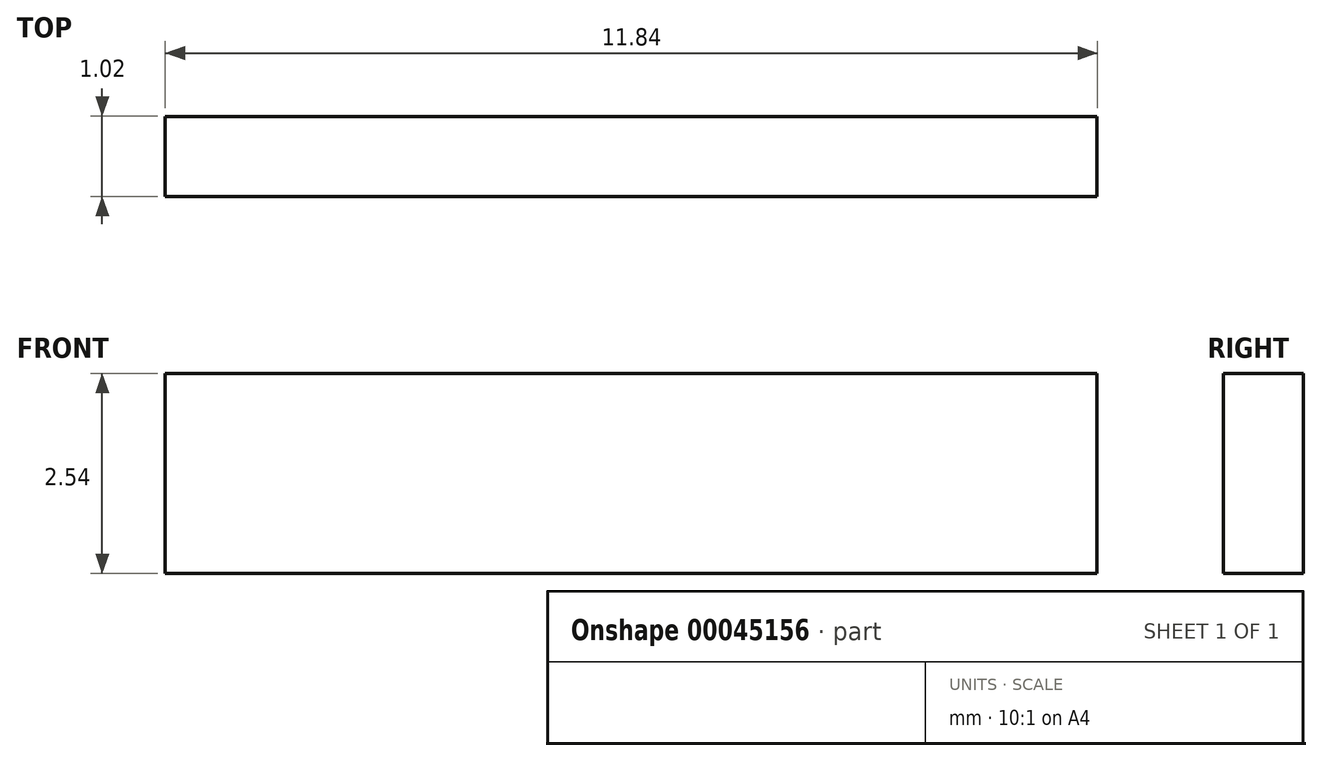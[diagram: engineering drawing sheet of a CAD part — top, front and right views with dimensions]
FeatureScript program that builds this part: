
annotation { "Feature Type Name" : "Feature", "Feature Type Description" : "" }
export const myFeature = defineFeature(function(context is Context, id is Id, definition is map)
    precondition{}
    {
        {
            var Q0;
            Q0=qCreatedBy(makeId("Top.planeOp"),FACE);
            var sketch = newSketch(context, id + "F0", { "sketchPlane" : qUnion([Q0])});
            skLineSegment(sketch, "E0", {"start": v(0, 0) * mm, "end": v(11.84, 0) * mm});
            skLineSegment(sketch, "E1", {"start": v(11.84, 0) * mm, "end": v(11.84, 1.02) * mm});
            skLineSegment(sketch, "E2", {"start": v(11.84, 1.02) * mm, "end": v(0, 1.02) * mm});
            skLineSegment(sketch, "E3", {"start": v(0, 1.02) * mm, "end": v(0, 0) * mm});
            skSolve(sketch);
        }
        {
            var Q0;
            Q0 = qSketchRegion(id + "F0", true);
            extrude(context, id + "F1", {"entities" : qUnion([Q0]), "depth" : 2.54 * mm});
        }
    });
